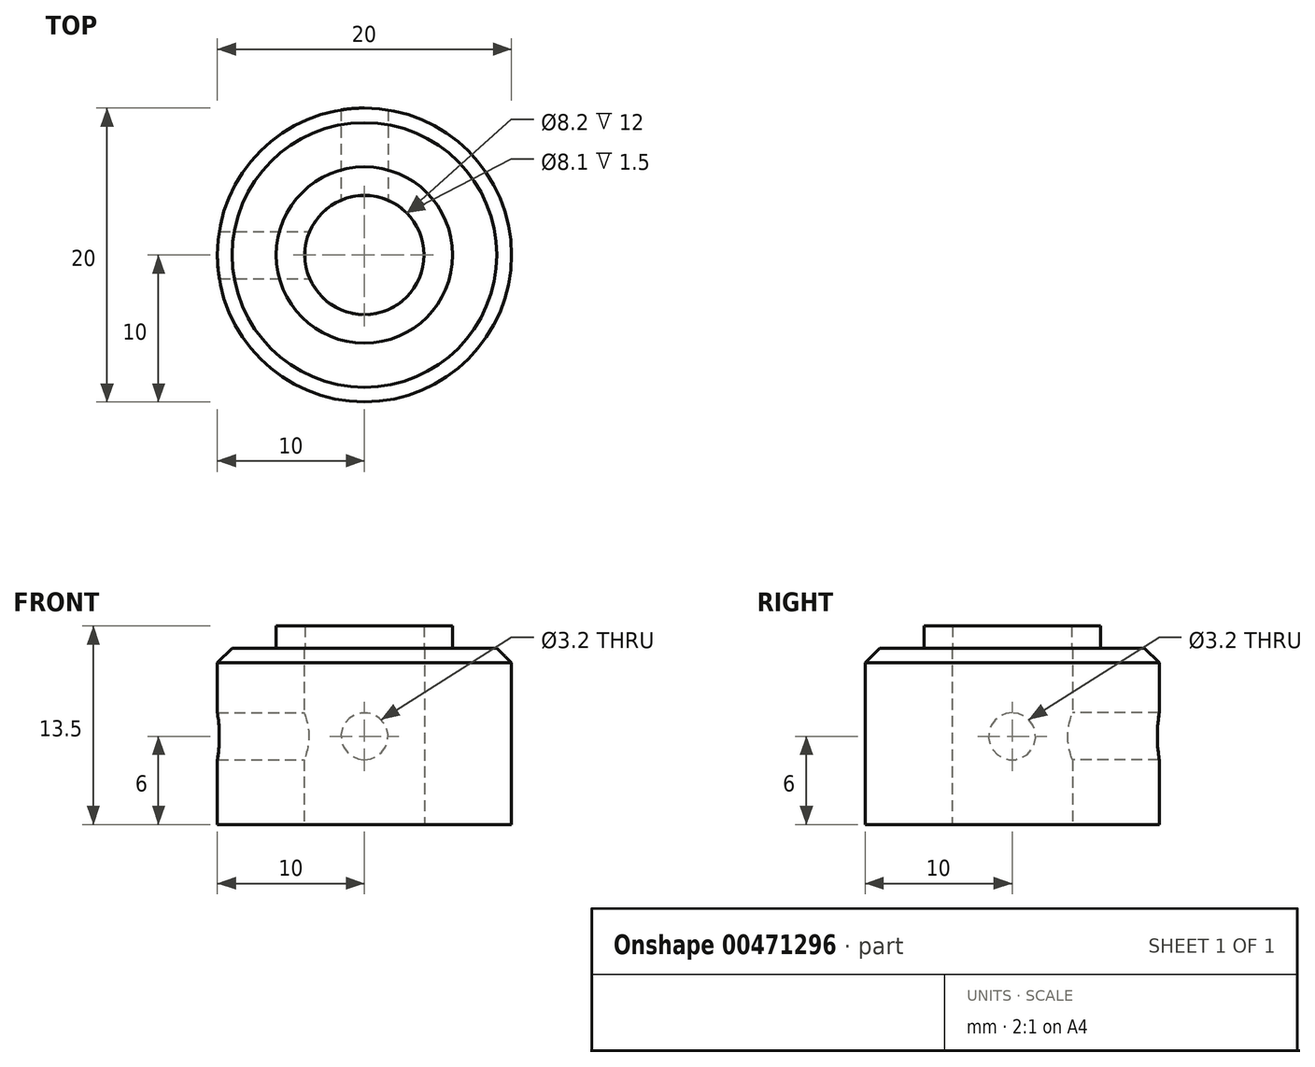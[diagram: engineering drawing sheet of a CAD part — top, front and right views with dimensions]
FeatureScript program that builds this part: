
annotation { "Feature Type Name" : "Feature", "Feature Type Description" : "" }
export const myFeature = defineFeature(function(context is Context, id is Id, definition is map)
    precondition{}
    {
        {
            var Q0;
            Q0=qCreatedBy(makeId("Top.planeOp"),FACE);
            var sketch = newSketch(context, id + "F0", { "sketchPlane" : qUnion([Q0])});
            skCircle(sketch, "E0", {"center": v(0, 0) * mm, "radius": 10 * mm});
            skCircle(sketch, "E1", {"center": v(0, 0) * mm, "radius": 4.1 * mm});
            skSolve(sketch);
        }
        {
            var Q0;
            Q0 = qSketchRegion(id + "F0", true);
            extrude(context, id + "F1", {"entities" : qUnion([Q0]), "depth" : 12 * mm});
        }
        {
            var Q0;
            Q0=qCreatedBy(makeId("Front.planeOp"),FACE);
            var sketch = newSketch(context, id + "F2", { "sketchPlane" : qUnion([Q0])});
            skCircle(sketch, "E2", {"center": v(0, 6) * mm, "radius": 1.6 * mm});
            skSolve(sketch);
        }
        {
            var Q0;
            Q0 = qSketchRegion(id + "F2", true);
            extrude(context, id + "F3", {"entities" : qUnion([Q0]), "operationType" : NewBodyOperationType.REMOVE, "oppositeDirection" : true, "depth" : 25 * mm});
        }
        {
            var Q0;
            Q0=qCreatedBy(makeId("Right.planeOp"),FACE);
            var sketch = newSketch(context, id + "F4", { "sketchPlane" : qUnion([Q0])});
            skCircle(sketch, "E3", {"center": v(0, 6) * mm, "radius": 1.6 * mm});
            skSolve(sketch);
        }
        {
            var Q0;
            Q0 = qSketchRegion(id + "F4", true);
            extrude(context, id + "F5", {"entities" : qUnion([Q0]), "operationType" : NewBodyOperationType.REMOVE, "oppositeDirection" : true, "depth" : 25 * mm});
        }
        {
            var Q0;
            Q0=makeQuery(id+"F1.opExtrude","CAP_FACE",FACE,{"disambiguationData":[OSD([sQuery(id+"F0.wireOp",EDGE,"E0"),sQuery(id+"F0.wireOp",EDGE,"E1")])],"isStart":false});
            var sketch = newSketch(context, id + "F6", { "sketchPlane" : qUnion([Q0])});
            skCircle(sketch, "E4", {"center": v(0, 0) * mm, "radius": 6 * mm});
            skCircle(sketch, "E5", {"center": v(0, 0) * mm, "radius": 4.05 * mm});
            skSolve(sketch);
        }
        {
            var Q0;
            Q0 = qSketchRegion(id + "F6", true);
            extrude(context, id + "F7", {"entities" : qUnion([Q0]), "operationType" : NewBodyOperationType.ADD, "depth" : 1.5 * mm});
        }
        {
            var Q0;
            Q0=makeQuery(id+"F1.opExtrude","CAP_EDGE",EDGE,{"disambiguationData":[OSD([sQuery(id+"F0.wireOp",EDGE,"E0")])],"isStart":false});
            chamfer(context, id + "F8", {"entities" : qUnion([Q0]), "width" : 1 * mm, "tangentPropagation" : true});
        }
    });
